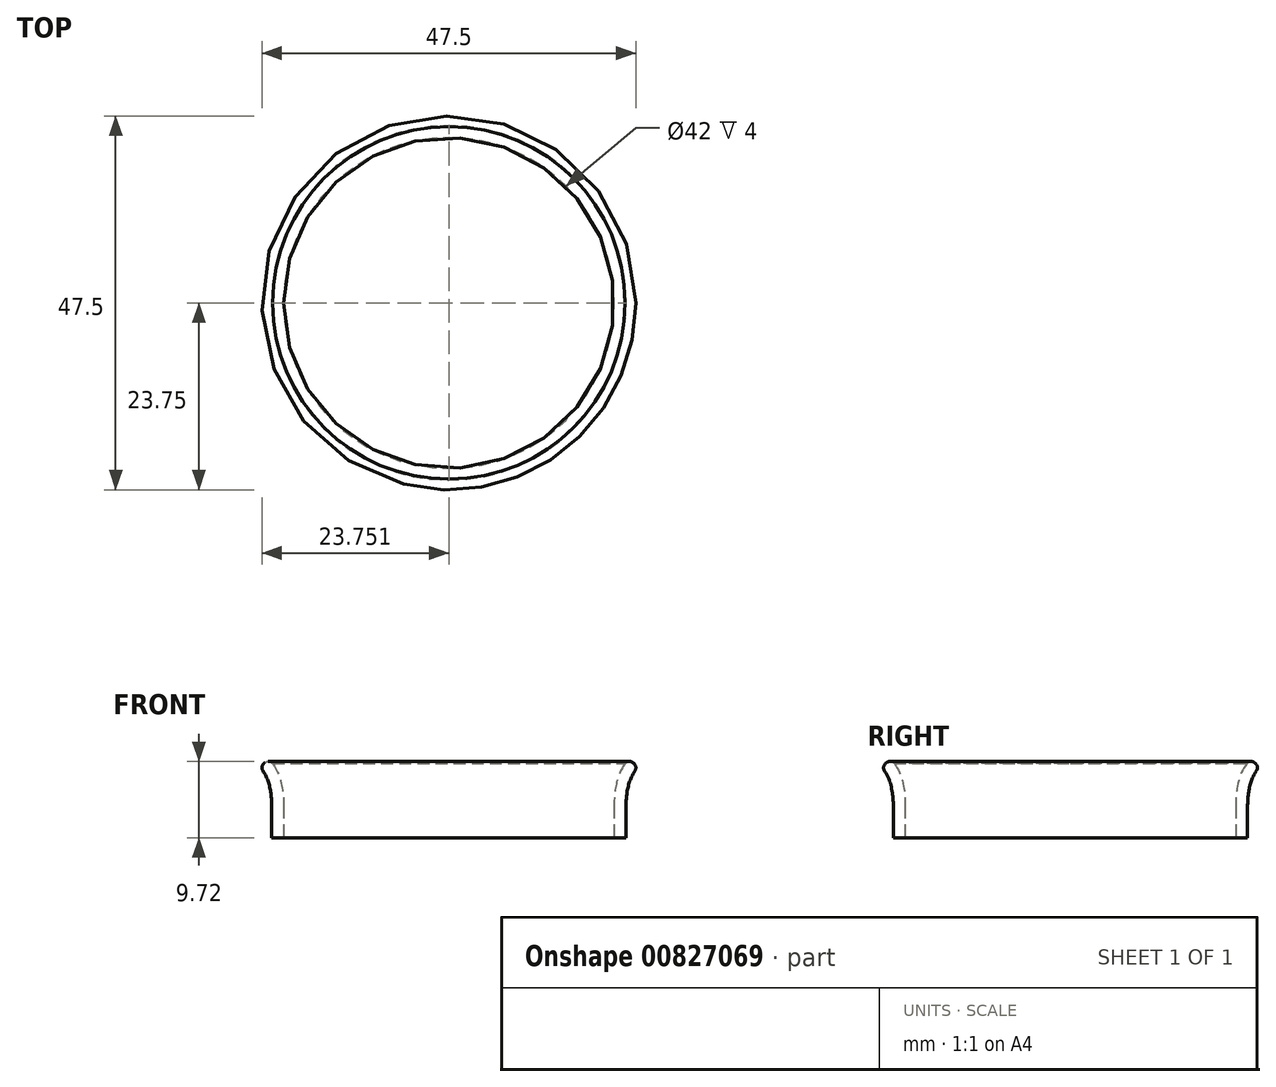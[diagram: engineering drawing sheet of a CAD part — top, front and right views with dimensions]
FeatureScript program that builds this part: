
annotation { "Feature Type Name" : "Feature", "Feature Type Description" : "" }
export const myFeature = defineFeature(function(context is Context, id is Id, definition is map)
    precondition{}
    {
        {
            var Q0;
            Q0=qCreatedBy(makeId("Top.planeOp"),FACE);
            var sketch = newSketch(context, id + "F0", { "sketchPlane" : qUnion([Q0])});
            skCircle(sketch, "E0", {"center": v(-32.46, 17.76) * mm, "radius": 20 * mm, "construction": true});
            skLineSegment(sketch, "E1", {"start": v(-32.46, 17.76) * mm, "end": v(0, 0) * mm, "construction": true});
            skLineSegment(sketch, "E2.bottom", {"start": v(10.5, 10.5) * mm, "end": v(-10.5, 10.5) * mm, "construction": true});
            skLineSegment(sketch, "E2.top", {"start": v(10.5, -10.5) * mm, "end": v(-10.5, -10.5) * mm, "construction": true});
            skLineSegment(sketch, "E2.left", {"start": v(10.5, 10.5) * mm, "end": v(10.5, -10.5) * mm, "construction": true});
            skLineSegment(sketch, "E2.right", {"start": v(-10.5, 10.5) * mm, "end": v(-10.5, -10.5) * mm, "construction": true});
            skPoint(sketch, "E2.middle", {"position": v(0, 0) * mm});
            skLineSegment(sketch, "E3.bottom", {"start": v(8, 12.5) * mm, "end": v(-8, 12.5) * mm, "construction": true});
            skLineSegment(sketch, "E3.top", {"start": v(8, 22.5) * mm, "end": v(-8, 22.5) * mm, "construction": true});
            skLineSegment(sketch, "E3.left", {"start": v(8, 12.5) * mm, "end": v(8, 22.5) * mm, "construction": true});
            skLineSegment(sketch, "E3.right", {"start": v(-8, 12.5) * mm, "end": v(-8, 22.5) * mm, "construction": true});
            skPoint(sketch, "E3.middle", {"position": v(0, 17.5) * mm});
            skCircle(sketch, "E4", {"center": v(0, 0) * mm, "radius": 37 * mm, "construction": true});
            skEllipse(sketch, "E5", {"center": v(-19, -31.75) * mm, "majorRadius": 20 * mm, "minorRadius": 17.3 * mm, "majorAxis": v(0, 1), "construction": true});
            skCircle(sketch, "E6", {"center": v(-32.46, 17.76) * mm, "radius": 21 * mm});
            skCircle(sketch, "E7", {"center": v(-32.46, 17.76) * mm, "radius": 22.5 * mm});
            skLineSegment(sketch, "E8", {"start": v(-19, -31.75) * mm, "end": v(-19, 0) * mm, "construction": true});
            skSolve(sketch);
        }
        {
            var Q0;
            Q0=makeQuery(id+"F0.imprint","IMPRINT",FACE,{"disambiguationData":[TD([[makeQuery(id+"F0.imprint","IMPRINT",EDGE,{"derivedFrom":sQuery(id+"F0.wireOp",EDGE,"E6")}),-1.0]])]});
            extrude(context, id + "F1", {"entities" : qUnion([Q0]), "depth" : 12 * mm, "offsetDistance" : 25 * mm, "hasSecondDirection" : true, "secondDirectionOppositeDirection" : false, "secondDirectionDepth" : 8 * mm});
        }
        {
            var Q0;
            Q0=makeQuery(id+"F1.opExtrude","CAP_FACE",FACE,{"disambiguationData":[OSD([sQuery(id+"F0.wireOp",EDGE,"E6"),sQuery(id+"F0.wireOp",EDGE,"E7")])],"isStart":false});
            var sketch = newSketch(context, id + "F2", { "sketchPlane" : qUnion([Q0])});
            skLineSegment(sketch, "E9", {"start": v(-32.46, 17.76) * mm, "end": v(-9.96, 17.76) * mm});
            skSolve(sketch);
        }
        {
            var Q0;
            Q0=sQuery(id+"F2.wireOp",EDGE,"E9");
            extrude(context, id + "F3", {"bodyType" : ToolBodyType.SURFACE, "surfaceEntities" : qUnion([Q0]), "depth" : 5 * mm, "offsetDistance" : 25 * mm});
        }
        {
            var Q0;
            Q0=makeQuery(id+"F3.opExtrude","SWEPT_FACE",FACE,{"disambiguationData":[OSD([sQuery(id+"F2.wireOp",EDGE,"E9")])]});
            var sketch = newSketch(context, id + "F4", { "sketchPlane" : qUnion([Q0])});
            skLineSegment(sketch, "E10", {"start": v(-9.96, 17) * mm, "end": v(-8.46, 17) * mm, "construction": true});
            skFitSpline(sketch, "E11", {"points": [v(-8.46, 17) * mm, v(-9.96, 12) * mm], "startDerivative": vector(-3.75, -4.1) * mm, "endDerivative": vector(0, -4.57) * mm});
            skFitSpline(sketch, "E12.0", {"points": [v(-9.57, 18.01) * mm, v(-10, 17.55) * mm, v(-10.65, 16.52) * mm, v(-11.18, 14.9) * mm, v(-11.42, 13.35) * mm, v(-11.46, 12.42) * mm, v(-11.46, 12) * mm]});
            skLineSegment(sketch, "E13.0", {"start": v(-53.46, 7) * mm, "end": v(-11.46, 7) * mm});
            skLineSegment(sketch, "E14", {"start": v(-9.57, 18.01) * mm, "end": v(-8.46, 17) * mm});
            skSolve(sketch);
        }
        {
            var Q0;
            {var subQ6=makeQuery(id+"F3.opExtrude","SWEPT_EDGE",EDGE,{"disambiguationData":[OSD([sQuery(id+"F2.wireOp",VERTEX,"E9.end")])]});Q0=makeQuery(id+"F4.imprint","IMPRINT",FACE,{"disambiguationData":[TD([[makeQuery(id+"F4.imprint","IMPRINT",EDGE,{"derivedFrom":subQ6}),1.0]])]});}
            var Q1;
            Q1=makeQuery(id+"F4.imprint","IMPRINT",FACE,{"disambiguationData":[TD([[makeQuery(id+"F4.imprint","IMPRINT",EDGE,{"derivedFrom":sQuery(id+"F4.wireOp",EDGE,"E11")}),-1.0]])]});
            var Q2;
            Q2=makeQuery(id+"F3.opExtrude","SWEPT_EDGE",EDGE,{"disambiguationData":[OSD([sQuery(id+"F2.wireOp",VERTEX,"E9.start")])]});
            revolve(context, id + "F5", {"operationType" : NewBodyOperationType.ADD, "surfaceOperationType" : NewSurfaceOperationType.NEW, "entities" : qUnion([Q0, Q1]), "axis" : qUnion([Q2]), "revolveType" : RevolveType.FULL});
        }
        {
            var Q0;
            Q0=makeQuery(id+"F5.opRevolve","SWEPT_EDGE",EDGE,{"disambiguationData":[OSD([sQuery(id+"F4.wireOp",EDGE,"E12.0"),sQuery(id+"F4.wireOp",EDGE,"E14")])]});
            var Q1;
            Q1=makeQuery(id+"F5.opRevolve","SWEPT_EDGE",EDGE,{"disambiguationData":[OSD([sQuery(id+"F4.wireOp",EDGE,"E11"),sQuery(id+"F4.wireOp",EDGE,"E14")])]});
            fillet(context, id + "F6", {"entities" : qUnion([Q0, Q1]), "radius" : 0.7 * mm, "tangentPropagation" : true, "allowEdgeOverflow" : false});
        }
        {
            var Q0;
            Q0=qCreatedBy(makeId("Front.planeOp"),FACE);
            var sketch = newSketch(context, id + "F7", { "sketchPlane" : qUnion([Q0])});
            skLineSegment(sketch, "E15", {"start": v(0, 0) * mm, "end": v(0, 5) * mm, "construction": true});
            skLineSegment(sketch, "E16", {"start": v(0, 5) * mm, "end": v(-19, 15.97) * mm, "construction": true});
            skLineSegment(sketch, "E17", {"start": v(-19, 15.97) * mm, "end": v(-23, 9.04) * mm, "construction": true});
            skLineSegment(sketch, "E18", {"start": v(-23, 9.04) * mm, "end": v(-5.68, -0.96) * mm, "construction": true});
            skLineSegment(sketch, "E19", {"start": v(-5.68, -0.96) * mm, "end": v(-40.32, 19.04) * mm});
            skSolve(sketch);
        }
        {
            var Q0;
            Q0=sQuery(id+"F7.wireOp",EDGE,"E19");
            extrude(context, id + "F8", {"bodyType" : ToolBodyType.SURFACE, "surfaceEntities" : qUnion([Q0]), "depth" : 50 * mm, "offsetDistance" : 25 * mm});
        }
    });
